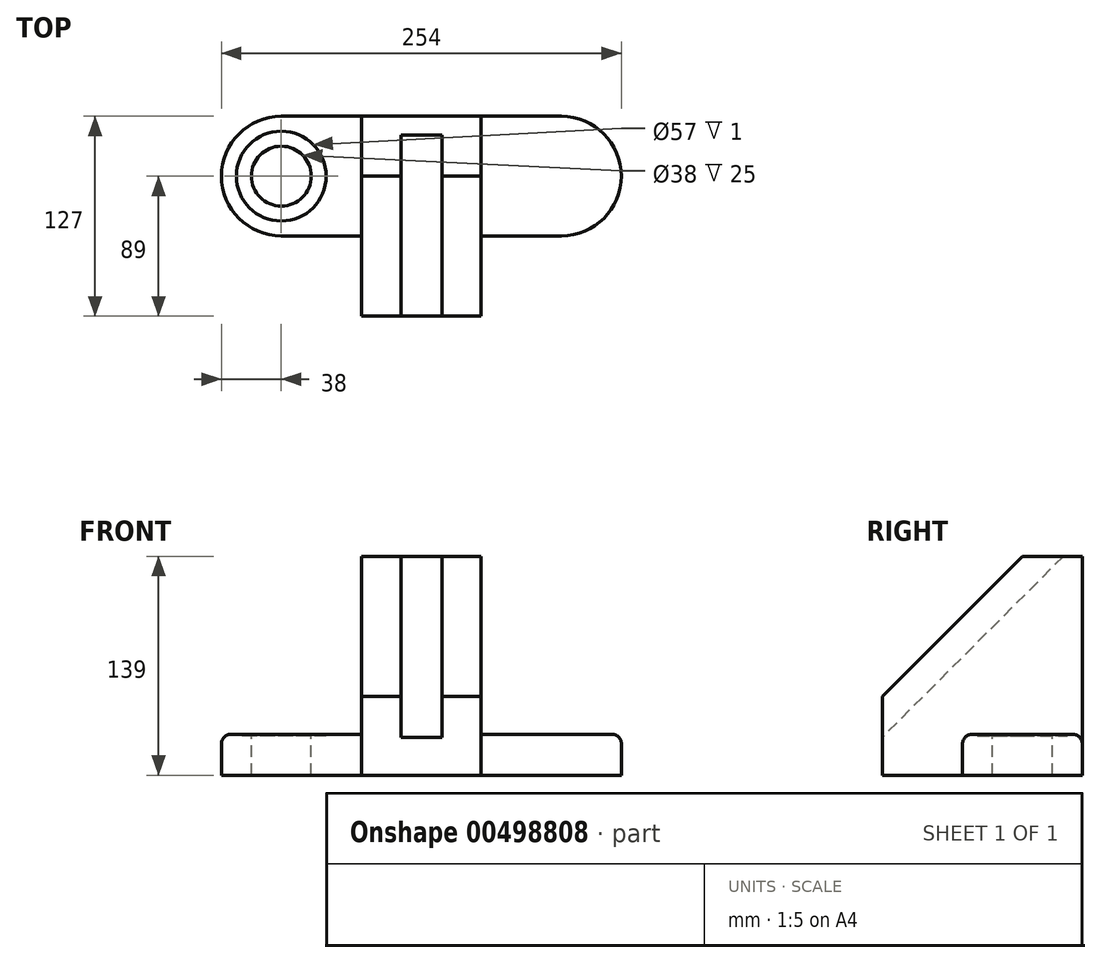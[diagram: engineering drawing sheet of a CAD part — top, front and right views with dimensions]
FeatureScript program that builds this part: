
annotation { "Feature Type Name" : "Feature", "Feature Type Description" : "" }
export const myFeature = defineFeature(function(context is Context, id is Id, definition is map)
    precondition{}
    {
        {
            var Q0;
            Q0=qCreatedBy(makeId("Right.planeOp"),FACE);
            var sketch = newSketch(context, id + "F0", { "sketchPlane" : qUnion([Q0])});
            skLineSegment(sketch, "E0", {"start": v(0, 0) * mm, "end": v(0, 139) * mm});
            skLineSegment(sketch, "E1", {"start": v(0, 139) * mm, "end": v(-38, 139) * mm});
            skLineSegment(sketch, "E2", {"start": v(-38, 139) * mm, "end": v(-127, 50) * mm});
            skLineSegment(sketch, "E3", {"start": v(-127, 50) * mm, "end": v(-127, 0) * mm});
            skLineSegment(sketch, "E4", {"start": v(-127, 0) * mm, "end": v(0, 0) * mm});
            skSolve(sketch);
        }
        {
            var Q0;
            Q0 = qSketchRegion(id + "F0", true);
            extrude(context, id + "F1", {"entities" : qUnion([Q0]), "endBound" : BoundingType.SYMMETRIC, "depth" : 76 * mm});
        }
        {
            var Q0;
            Q0=qCreatedBy(makeId("Right.planeOp"),FACE);
            var sketch = newSketch(context, id + "F2", { "sketchPlane" : qUnion([Q0])});
            skLineSegment(sketch, "E5", {"start": v(-12, 139) * mm, "end": v(-127, 24) * mm});
            skLineSegment(sketch, "E6", {"start": v(-127, 24) * mm, "end": v(-127, 50) * mm});
            skLineSegment(sketch, "E7", {"start": v(-127, 50) * mm, "end": v(-38, 139) * mm});
            skLineSegment(sketch, "E8", {"start": v(-38, 139) * mm, "end": v(-12, 139) * mm});
            skSolve(sketch);
        }
        {
            var Q0;
            Q0 = qSketchRegion(id + "F2", true);
            extrude(context, id + "F3", {"entities" : qUnion([Q0]), "operationType" : NewBodyOperationType.REMOVE, "endBound" : BoundingType.SYMMETRIC, "oppositeDirection" : true, "depth" : 26 * mm});
        }
        {
            var Q0;
            Q0=qCreatedBy(makeId("Top.planeOp"),FACE);
            var sketch = newSketch(context, id + "F4", { "sketchPlane" : qUnion([Q0])});
            skLineSegment(sketch, "E9", {"start": v(-89, -38) * mm, "end": v(89, -38) * mm, "construction": true});
            skPoint(sketch, "E10", {"position": v(0, -38) * mm});
            skArc(sketch, "E11.0.startCap", {"start": v(-89, -76) * mm, "mid": v(-127, -38) * mm, "end": v(-89, 0) * mm});
            skArc(sketch, "E11.0.endCap", {"start": v(89, 0) * mm, "mid": v(127, -38) * mm, "end": v(89, -76) * mm});
            skLineSegment(sketch, "E11.0.left", {"start": v(-89, 0) * mm, "end": v(89, 0) * mm});
            skLineSegment(sketch, "E11.0.right", {"start": v(-89, -76) * mm, "end": v(89, -76) * mm});
            skSolve(sketch);
        }
        {
            var Q0;
            Q0 = qSketchRegion(id + "F4", true);
            extrude(context, id + "F5", {"entities" : qUnion([Q0]), "operationType" : NewBodyOperationType.ADD, "depth" : 26 * mm});
        }
        {
            var Q0;
            {var subQ0=sQuery(id+"F4.wireOp",EDGE,"E11.0.startCap");var subQ1=sQuery(id+"F4.wireOp",EDGE,"E11.0.left");var subQ3=sQuery(id+"F4.wireOp",EDGE,"E11.0.right");Q0=makeQuery(id+"F5.boolean.opBoolean","SPLIT",FACE,{"disambiguationData":[TD([makeQuery(id+"F5.opExtrude","SWEPT_FACE",FACE,{"disambiguationData":[OSD([subQ0])]})])],"derivedFrom":makeQuery(id+"F5.opExtrude","CAP_FACE",FACE,{"disambiguationData":[OSD([subQ0,sQuery(id+"F4.wireOp",EDGE,"E11.0.endCap"),subQ1,subQ3])],"isStart":false})});}
            var sketch = newSketch(context, id + "F6", { "sketchPlane" : qUnion([Q0])});
            skCircle(sketch, "E12", {"center": v(-89, -38) * mm, "radius": 28.5 * mm});
            skSolve(sketch);
        }
        {
            var Q0;
            Q0 = qSketchRegion(id + "F6", true);
            extrude(context, id + "F7", {"entities" : qUnion([Q0]), "operationType" : NewBodyOperationType.REMOVE, "oppositeDirection" : true, "depth" : 1 * mm});
        }
        {
            var Q0;
            Q0=makeQuery(id+"F7.boolean.opBoolean","COPY",FACE,{"derivedFrom":makeQuery(id+"F7.opExtrude","CAP_FACE",FACE,{"disambiguationData":[OSD([sQuery(id+"F6.wireOp",EDGE,"E12")])],"isStart":false})});
            var sketch = newSketch(context, id + "F8", { "sketchPlane" : qUnion([Q0])});
            skCircle(sketch, "E13", {"center": v(-89, -38) * mm, "radius": 19 * mm});
            skSolve(sketch);
        }
        {
            var Q0;
            Q0 = qSketchRegion(id + "F8", true);
            extrude(context, id + "F9", {"entities" : qUnion([Q0]), "operationType" : NewBodyOperationType.REMOVE, "endBound" : BoundingType.UP_TO_NEXT, "oppositeDirection" : true, "depth" : 25 * mm});
        }
        {
            var Q0;
            {var subQ0=sQuery(id+"F4.wireOp",EDGE,"E11.0.startCap");var subQ1=sQuery(id+"F4.wireOp",EDGE,"E11.0.right");Q0=makeQuery(id+"F5.boolean.opBoolean","SPLIT",EDGE,{"disambiguationData":[TD([makeQuery(id+"F5.opExtrude","SWEPT_FACE",FACE,{"disambiguationData":[OSD([subQ0])]})])],"derivedFrom":makeQuery(id+"F5.opExtrude","CAP_EDGE",EDGE,{"disambiguationData":[OSD([subQ1])],"isStart":false})});}
            var Q1;
            {var subQ0=sQuery(id+"F4.wireOp",EDGE,"E11.0.left");var subQ1=sQuery(id+"F4.wireOp",EDGE,"E11.0.endCap");Q1=makeQuery(id+"F5.boolean.opBoolean","SPLIT",EDGE,{"disambiguationData":[TD([makeQuery(id+"F5.opExtrude","SWEPT_FACE",FACE,{"disambiguationData":[OSD([subQ1])]})])],"derivedFrom":makeQuery(id+"F5.opExtrude","CAP_EDGE",EDGE,{"disambiguationData":[OSD([subQ0])],"isStart":false})});}
            fillet(context, id + "F10", {"entities" : qUnion([Q0, Q1]), "radius" : 6 * mm, "tangentPropagation" : true, "allowEdgeOverflow" : false});
        }
    });
